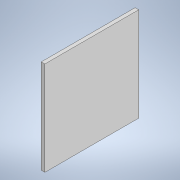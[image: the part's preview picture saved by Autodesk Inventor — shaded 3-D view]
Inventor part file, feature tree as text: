
AUTODESK INVENTOR PART (.ipt)
format: ipt  version: 2021 (Build 250183000, 183)  size: 86,528 bytes
history: native  units: mm
features: extrude x1, sketch x1
ambient origin geometry x8: Origin, YZ Plane, XZ Plane, XY Plane, X Axis, Y Axis, Z Axis, Center Point
bodies: Solid1 (feature_tree)
feature tree (2):
  extrude  "Extrusion1"  Depth=65.0mm
  sketch  "Sketch1"  dims[d0=65.0mm d1=65.0mm d2=2.5mm d3=0.0mm]
